# Revit family: Runtal-RC-1
name_source: partatom
category: Generic Models
units: mm (PartAtom-declared; Revit-internal decimal feet)

## family parameters
Always vertical = Yes
Can host rebar = No
Cut with Voids When Loaded = No
Host = Ceiling
Maintain Annotation Orientation = No
Part Type = Normal
Room Calculation Point = No
Round Connector Dimension = Use Diameter
Shared = No

## types (1)
- Runtal-RC-1
    Assembly Code = D3020
    Default Elevation = 0' - 0"
    Description = RC panel radiators are manufactured in the USA from cold rolled steel and ceiling mounted. The panels are finished in a gloss powdercoat, and are available in many standard colors and over 100 optional colors. These panels are made in lengths from 2’-0” to 29’-6”, and widths from 3” to 70”. Standard piping connections are 1/2” NPT for inlet and outlet piping, and 1/8” NPT for vents (3/4” NPT inlets and outlets are available by special order). For more complete RC panel specifications, please refer to the Runtal technical pages.
    Length = 1' - 8"
    Manufacturer = Runtal Radiators
    Model = RC-5
    Radiator = Steel, Paint Finish, Ivory, Glossy
    URL = http://www.runtalnorthamerica.com

## geometry (parser evidence)
native form markers: Sweep x31
no freeform markers — native parametric forms only
